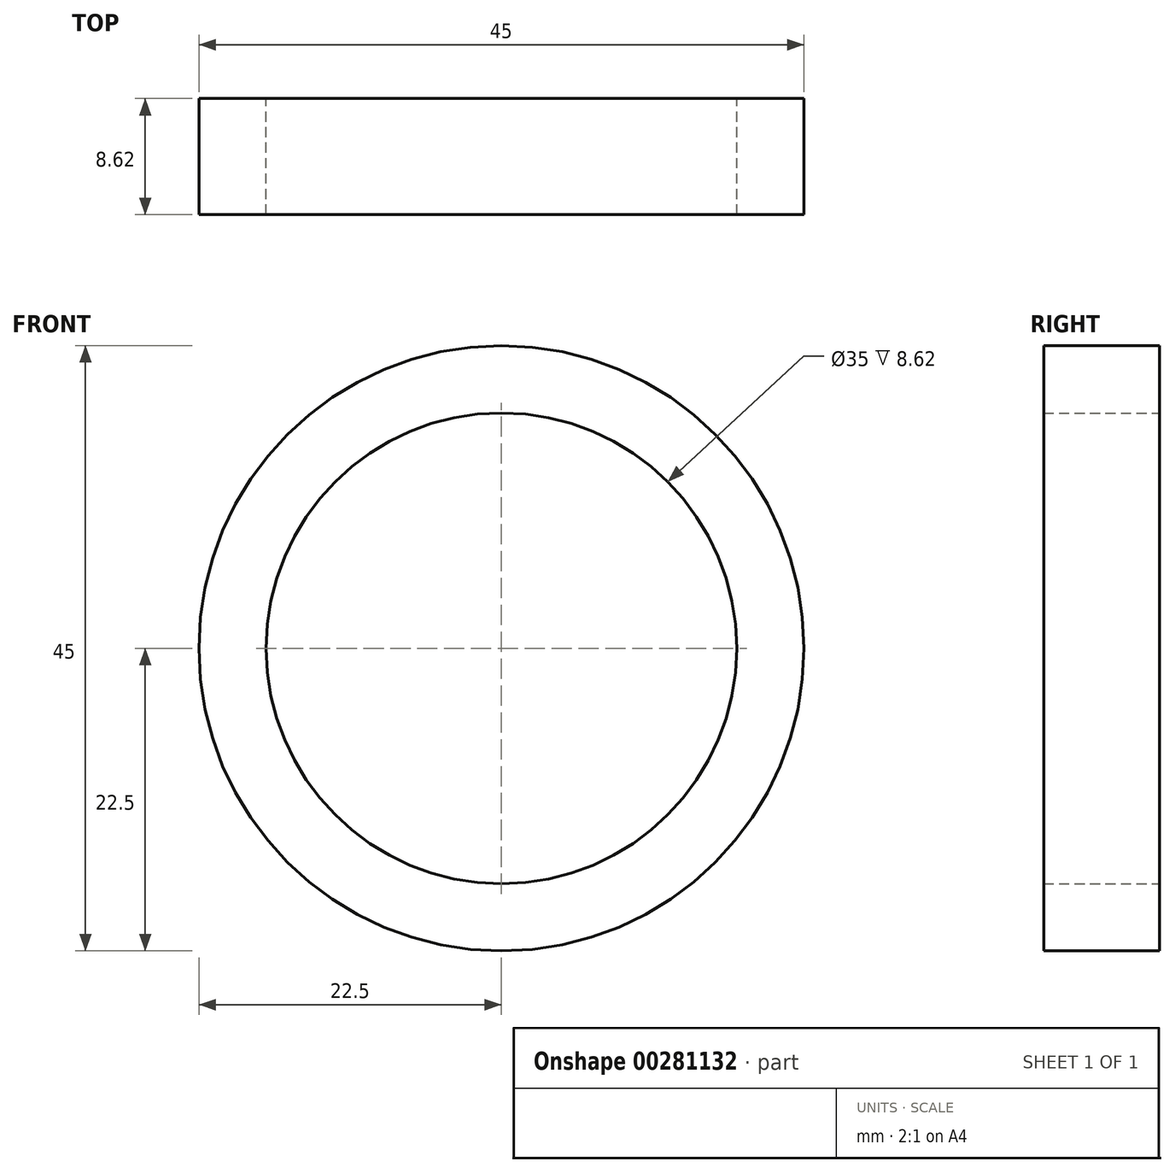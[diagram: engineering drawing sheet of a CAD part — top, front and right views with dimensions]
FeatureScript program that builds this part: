
annotation { "Feature Type Name" : "Feature", "Feature Type Description" : "" }
export const myFeature = defineFeature(function(context is Context, id is Id, definition is map)
    precondition{}
    {
        {
            var Q0;
            Q0=qCreatedBy(makeId("Front.planeOp"),FACE);
            var sketch = newSketch(context, id + "F0", { "sketchPlane" : qUnion([Q0])});
            skCircle(sketch, "E0", {"center": v(0, 0) * mm, "radius": 17.5 * mm});
            skCircle(sketch, "E1", {"center": v(0, 0) * mm, "radius": 22.5 * mm});
            skSolve(sketch);
        }
        {
            var Q0;
            Q0=makeQuery(id+"F0.imprint","IMPRINT",FACE,{"disambiguationData":[TD([[makeQuery(id+"F0.imprint","IMPRINT",EDGE,{"derivedFrom":sQuery(id+"F0.wireOp",EDGE,"E0")}),-1.0]])]});
            extrude(context, id + "F1", {"entities" : qUnion([Q0]), "depth" : 8.62 * mm});
        }
    });
